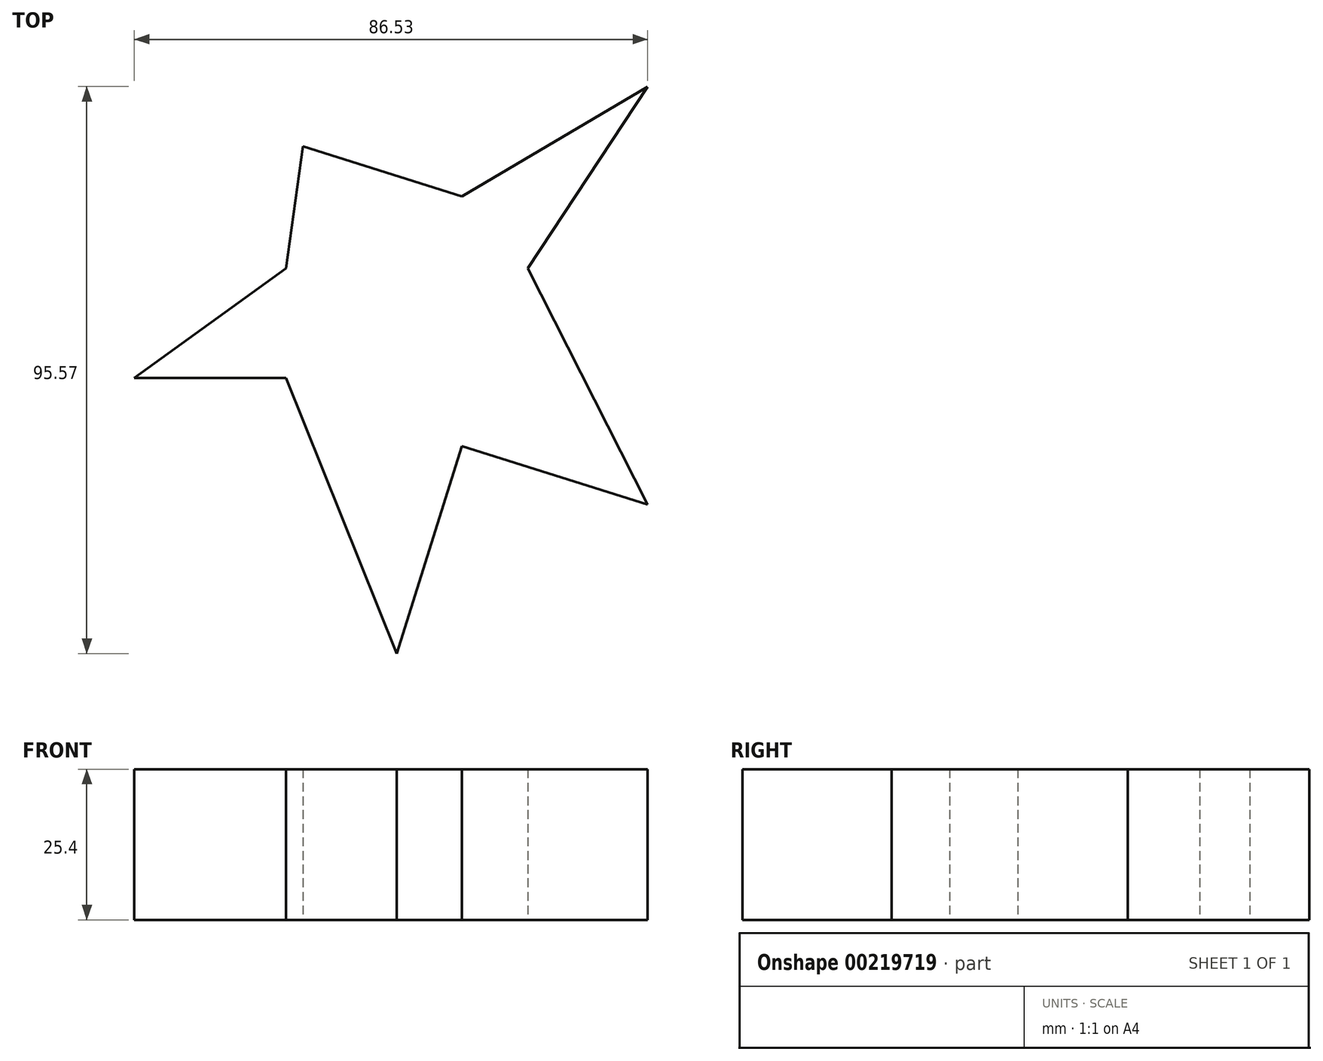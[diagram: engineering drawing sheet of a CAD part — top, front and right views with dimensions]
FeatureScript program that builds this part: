
annotation { "Feature Type Name" : "Feature", "Feature Type Description" : "" }
export const myFeature = defineFeature(function(context is Context, id is Id, definition is map)
    precondition{}
    {
        {
            var Q0;
            Q0=qCreatedBy(makeId("Top.planeOp"),FACE);
            var sketch = newSketch(context, id + "F0", { "sketchPlane" : qUnion([Q0])});
            skLineSegment(sketch, "E0", {"start": v(0, 0) * mm, "end": v(10.97, 34.95) * mm});
            skLineSegment(sketch, "E1", {"start": v(10.97, 34.95) * mm, "end": v(42.29, 25.12) * mm});
            skLineSegment(sketch, "E2", {"start": v(42.29, 25.12) * mm, "end": v(22.1, 64.96) * mm});
            skLineSegment(sketch, "E3", {"start": v(22.1, 64.96) * mm, "end": v(42.29, 95.57) * mm});
            skLineSegment(sketch, "E4", {"start": v(42.29, 95.57) * mm, "end": v(10.97, 77.09) * mm});
            skLineSegment(sketch, "E5", {"start": v(10.97, 77.09) * mm, "end": v(-15.85, 85.5) * mm});
            skLineSegment(sketch, "E6", {"start": v(-15.85, 85.5) * mm, "end": v(-18.68, 64.96) * mm});
            skLineSegment(sketch, "E7", {"start": v(-18.68, 64.96) * mm, "end": v(-44.24, 46.44) * mm});
            skLineSegment(sketch, "E8", {"start": v(-44.24, 46.44) * mm, "end": v(-18.68, 46.44) * mm});
            skLineSegment(sketch, "E9", {"start": v(-18.68, 46.44) * mm, "end": v(0, 0) * mm});
            skSolve(sketch);
        }
        {
            var Q0;
            Q0=makeQuery(id+"F0.imprint","IMPRINT",FACE,{"disambiguationData":[TD([[makeQuery(id+"F0.imprint","IMPRINT",EDGE,{"derivedFrom":sQuery(id+"F0.wireOp",EDGE,"E0")}),1.0]])]});
            extrude(context, id + "F1", {"entities" : qUnion([Q0]), "depth" : 25.4 * mm});
        }
    });
